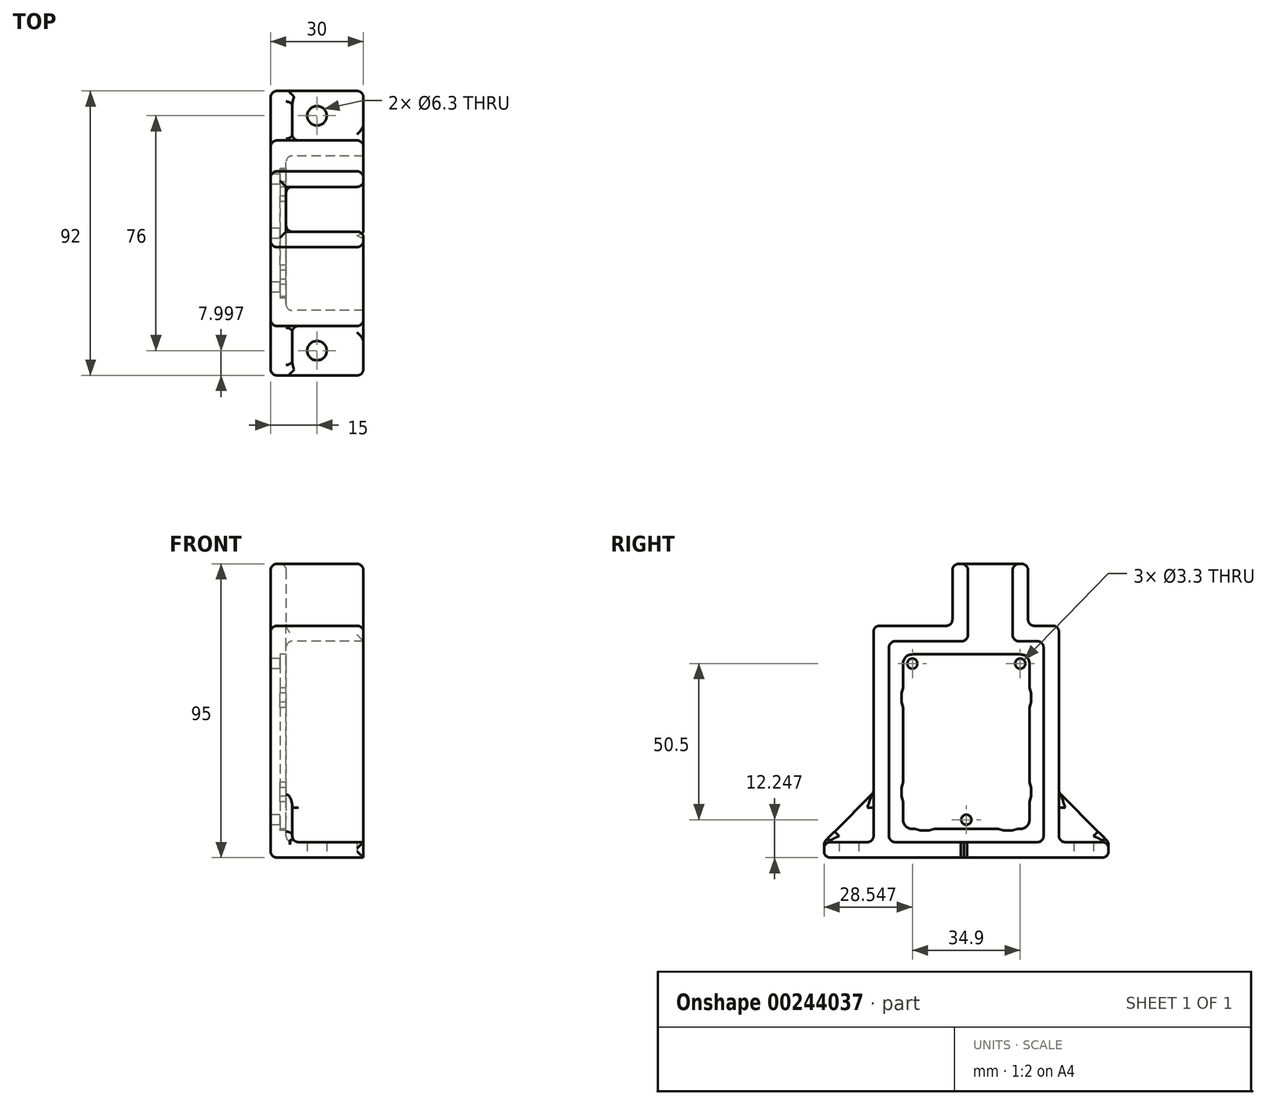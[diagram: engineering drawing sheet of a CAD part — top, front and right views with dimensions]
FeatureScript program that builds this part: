
annotation { "Feature Type Name" : "Feature", "Feature Type Description" : "" }
export const myFeature = defineFeature(function(context is Context, id is Id, definition is map)
    precondition{}
    {
        {
            var Q0;
            Q0=qCreatedBy(makeId("Right.planeOp"),FACE);
            var sketch = newSketch(context, id + "F0", { "sketchPlane" : qUnion([Q0])});
            skCircle(sketch, "E0", {"center": v(-16.66, 26.27) * mm, "radius": 3 * mm});
            skPoint(sketch, "E0.first.point", {"position": v(-14.03, 27.7) * mm});
            skPoint(sketch, "E0.second.point", {"position": v(-18.5, 23.89) * mm});
            skPoint(sketch, "E0.third.point", {"position": v(-19.66, 26.27) * mm});
            skCircle(sketch, "E1", {"center": v(-16.66, 26.27) * mm, "radius": 1.65 * mm});
            skCircle(sketch, "E2", {"center": v(18.24, 26.27) * mm, "radius": 3 * mm});
            skPoint(sketch, "E2.second.point", {"position": v(21.24, 26.27) * mm});
            skPoint(sketch, "E2.third.point", {"position": v(16.12, 24.15) * mm});
            skCircle(sketch, "E3", {"center": v(18.24, 26.27) * mm, "radius": 1.65 * mm});
            skCircle(sketch, "E4", {"center": v(0.79, -24.23) * mm, "radius": 3 * mm});
            skPoint(sketch, "E4.first.point", {"position": v(-0.78, -21.68) * mm});
            skPoint(sketch, "E4.second.point", {"position": v(3.71, -23.57) * mm});
            skPoint(sketch, "E4.third.point", {"position": v(-0.7, -26.84) * mm});
            skCircle(sketch, "E5", {"center": v(0.79, -24.23) * mm, "radius": 1.65 * mm});
            skLineSegment(sketch, "E6", {"start": v(-16.66, 26.27) * mm, "end": v(18.24, 26.27) * mm});
            skLineSegment(sketch, "E7", {"start": v(0.79, 26.27) * mm, "end": v(0.79, -24.23) * mm});
            skPoint(sketch, "E8", {"position": v(0.79, 1.02) * mm});
            skLineSegment(sketch, "E9.rect.bottom", {"start": v(30.79, 38.52) * mm, "end": v(-29.21, 38.52) * mm});
            skLineSegment(sketch, "E9.rect.top", {"start": v(30.79, -36.48) * mm, "end": v(-29.21, -36.48) * mm});
            skLineSegment(sketch, "E9.rect.left", {"start": v(30.79, 38.52) * mm, "end": v(30.79, -36.48) * mm});
            skLineSegment(sketch, "E9.rect.right", {"start": v(-29.21, 38.52) * mm, "end": v(-29.21, -36.48) * mm});
            skLineSegment(sketch, "E10.top", {"start": v(-13.71, 38.52) * mm, "end": v(0.79, 38.52) * mm});
            skLineSegment(sketch, "E11.bottom", {"start": v(6.79, 38.52) * mm, "end": v(0.79, 38.52) * mm});
            skLineSegment(sketch, "E12.bottom", {"start": v(-19.71, 38.52) * mm, "end": v(-13.71, 38.52) * mm});
            skSolve(sketch);
        }
        {
            var Q0;
            Q0=qCreatedBy(makeId("Right.planeOp"),FACE);
            var sketch = newSketch(context, id + "F1", { "sketchPlane" : qUnion([Q0])});
            skCircle(sketch, "E13", {"center": v(-16.66, 26.27) * mm, "radius": 3 * mm});
            skPoint(sketch, "E13.first.point", {"position": v(-14.03, 27.7) * mm});
            skPoint(sketch, "E13.second.point", {"position": v(-18.5, 23.89) * mm});
            skPoint(sketch, "E13.third.point", {"position": v(-19.66, 26.27) * mm});
            skCircle(sketch, "E14", {"center": v(-16.66, 26.27) * mm, "radius": 1.65 * mm});
            skLineSegment(sketch, "E15", {"start": v(-16.66, 29.27) * mm, "end": v(18.24, 29.27) * mm});
            skCircle(sketch, "E16", {"center": v(18.24, 26.27) * mm, "radius": 3 * mm});
            skPoint(sketch, "E16.second.point", {"position": v(21.24, 26.27) * mm});
            skPoint(sketch, "E16.third.point", {"position": v(16.12, 24.15) * mm});
            skCircle(sketch, "E17", {"center": v(18.24, 26.27) * mm, "radius": 1.65 * mm});
            skLineSegment(sketch, "E18", {"start": v(21.24, 26.27) * mm, "end": v(21.24, -24.23) * mm});
            skLineSegment(sketch, "E19", {"start": v(18.24, -27.23) * mm, "end": v(-16.66, -27.23) * mm});
            skLineSegment(sketch, "E20", {"start": v(-19.66, -24.23) * mm, "end": v(-19.66, 26.27) * mm});
            skCircle(sketch, "E21", {"center": v(0.79, -24.23) * mm, "radius": 3 * mm});
            skPoint(sketch, "E21.first.point", {"position": v(-0.78, -21.68) * mm});
            skPoint(sketch, "E21.second.point", {"position": v(3.71, -23.57) * mm});
            skPoint(sketch, "E21.third.point", {"position": v(-0.7, -26.84) * mm});
            skCircle(sketch, "E22", {"center": v(0.79, -24.23) * mm, "radius": 1.65 * mm});
            skCircle(sketch, "E23", {"center": v(-16.66, -24.23) * mm, "radius": 3 * mm});
            skPoint(sketch, "E23.third.point", {"position": v(-18.78, -26.35) * mm});
            skCircle(sketch, "E24", {"center": v(18.24, -24.23) * mm, "radius": 3 * mm});
            skPoint(sketch, "E24.third.point", {"position": v(20.85, -25.72) * mm});
            skLineSegment(sketch, "E25", {"start": v(12.81, -27.73) * mm, "end": v(15.66, -27.73) * mm});
            skLineSegment(sketch, "E26", {"start": v(12.81, -27.73) * mm, "end": v(11.08, -27.23) * mm});
            skLineSegment(sketch, "E27", {"start": v(15.66, -27.73) * mm, "end": v(17.4, -27.23) * mm});
            skLineSegment(sketch, "E28", {"start": v(-14.09, -27.73) * mm, "end": v(-11.24, -27.73) * mm});
            skLineSegment(sketch, "E29", {"start": v(-11.24, -27.73) * mm, "end": v(-9.5, -27.23) * mm});
            skLineSegment(sketch, "E30", {"start": v(-15.82, -27.23) * mm, "end": v(-14.09, -27.73) * mm});
            skLineSegment(sketch, "E31", {"start": v(-20.16, -13.8) * mm, "end": v(-19.66, -12.07) * mm});
            skLineSegment(sketch, "E32", {"start": v(-20.16, -13.8) * mm, "end": v(-20.16, -16.66) * mm});
            skLineSegment(sketch, "E33", {"start": v(-20.16, -16.66) * mm, "end": v(-19.66, -18.4) * mm});
            skLineSegment(sketch, "E34", {"start": v(-20.16, 16.7) * mm, "end": v(-20.16, 13.84) * mm});
            skLineSegment(sketch, "E35", {"start": v(-20.16, 13.84) * mm, "end": v(-19.66, 12.1) * mm});
            skLineSegment(sketch, "E36", {"start": v(-20.16, 16.7) * mm, "end": v(-19.66, 18.43) * mm});
            skLineSegment(sketch, "E37", {"start": v(21.74, 16.7) * mm, "end": v(21.24, 18.43) * mm});
            skLineSegment(sketch, "E38", {"start": v(21.74, 16.7) * mm, "end": v(21.74, 13.84) * mm});
            skLineSegment(sketch, "E39", {"start": v(21.74, 13.84) * mm, "end": v(21.24, 12.1) * mm});
            skLineSegment(sketch, "E40", {"start": v(21.24, -12.07) * mm, "end": v(21.74, -13.87) * mm});
            skLineSegment(sketch, "E41", {"start": v(21.74, -13.87) * mm, "end": v(21.74, -16.66) * mm});
            skLineSegment(sketch, "E42", {"start": v(21.74, -16.66) * mm, "end": v(21.24, -18.4) * mm});
            skLineSegment(sketch, "E43", {"start": v(-16.66, 26.27) * mm, "end": v(18.24, 26.27) * mm});
            skLineSegment(sketch, "E44", {"start": v(0.79, 26.27) * mm, "end": v(0.79, -24.23) * mm});
            skPoint(sketch, "E45", {"position": v(0.79, 1.02) * mm});
            skLineSegment(sketch, "E46.rect.bottom", {"start": v(30.79, 38.52) * mm, "end": v(-29.21, 38.52) * mm});
            skLineSegment(sketch, "E46.rect.top", {"start": v(30.79, -36.48) * mm, "end": v(-29.21, -36.48) * mm});
            skLineSegment(sketch, "E46.rect.left", {"start": v(30.79, 38.52) * mm, "end": v(30.79, -36.48) * mm});
            skLineSegment(sketch, "E46.rect.right", {"start": v(-29.21, 38.52) * mm, "end": v(-29.21, -36.48) * mm});
            skLineSegment(sketch, "E47.top", {"start": v(-13.71, 38.52) * mm, "end": v(0.79, 38.52) * mm});
            skLineSegment(sketch, "E48.bottom", {"start": v(6.79, 38.52) * mm, "end": v(0.79, 38.52) * mm});
            skLineSegment(sketch, "E49.bottom", {"start": v(-19.71, 38.52) * mm, "end": v(-13.71, 38.52) * mm});
            skSolve(sketch);
        }
        {
            var Q0;
            Q0 = qSketchRegion(id + "F0", true);
            var Q1;
            Q1=makeQuery(id+"F0.imprint","IMPRINT",FACE,{"disambiguationData":[TD([[makeQuery(id+"F0.imprint","IMPRINT",EDGE,{"derivedFrom":sQuery(id+"F0.wireOp",EDGE,"E4")}),1.0]])]});
            var Q2;
            Q2=makeQuery(id+"F0.imprint","IMPRINT",FACE,{"disambiguationData":[TD([[makeQuery(id+"F0.imprint","IMPRINT",EDGE,{"derivedFrom":sQuery(id+"F0.wireOp",EDGE,"E2")}),1.0]])]});
            var Q3;
            Q3=makeQuery(id+"F0.imprint","IMPRINT",FACE,{"disambiguationData":[TD([[makeQuery(id+"F0.imprint","IMPRINT",EDGE,{"derivedFrom":sQuery(id+"F0.wireOp",EDGE,"E0")}),1.0]])]});
            extrude(context, id + "F2", {"entities" : qUnion([Q0, Q1, Q2, Q3]), "offsetDistance" : 25 * mm, "depth" : 3 * mm});
        }
        {
            var Q0;
            Q0 = qSketchRegion(id + "F1", true);
            extrude(context, id + "F3", {"entities" : qUnion([Q0]), "operationType" : NewBodyOperationType.ADD, "offsetDistance" : 25 * mm, "depth" : 5 * mm});
        }
        {
            var Q0;
            Q0=makeQuery(id+"F2.opExtrude","CAP_FACE",FACE,{"disambiguationData":[OSD([sQuery(id+"F0.wireOp",EDGE,"E1"),sQuery(id+"F0.wireOp",EDGE,"E3"),sQuery(id+"F0.wireOp",EDGE,"E5"),sQuery(id+"F0.wireOp",EDGE,"E9.rect.bottom"),sQuery(id+"F0.wireOp",EDGE,"E9.rect.top"),sQuery(id+"F0.wireOp",EDGE,"E9.rect.left"),sQuery(id+"F0.wireOp",EDGE,"E9.rect.right"),sQuery(id+"F0.wireOp",EDGE,"E10.top"),sQuery(id+"F0.wireOp",EDGE,"E11.bottom"),sQuery(id+"F0.wireOp",EDGE,"E12.bottom")])],"isStart":true});
            var sketch = newSketch(context, id + "F4", { "sketchPlane" : qUnion([Q0])});
            skLineSegment(sketch, "E50.bottom", {"start": v(-30.79, 38.52) * mm, "end": v(-25.79, 38.52) * mm});
            skLineSegment(sketch, "E50.top", {"start": v(-30.79, -31.48) * mm, "end": v(-25.79, -31.48) * mm});
            skLineSegment(sketch, "E50.left", {"start": v(-30.79, 38.52) * mm, "end": v(-30.79, -31.48) * mm});
            skLineSegment(sketch, "E50.right", {"start": v(-25.79, 38.52) * mm, "end": v(-25.79, -31.48) * mm});
            skLineSegment(sketch, "E51.bottom", {"start": v(29.21, 38.52) * mm, "end": v(24.21, 38.52) * mm});
            skLineSegment(sketch, "E51.top", {"start": v(29.21, -31.48) * mm, "end": v(24.21, -31.48) * mm});
            skLineSegment(sketch, "E51.left", {"start": v(29.21, 38.52) * mm, "end": v(29.21, -31.48) * mm});
            skLineSegment(sketch, "E51.right", {"start": v(24.21, 38.52) * mm, "end": v(24.21, -31.48) * mm});
            skLineSegment(sketch, "E52.bottom", {"start": v(-30.79, -31.48) * mm, "end": v(29.21, -31.48) * mm});
            skLineSegment(sketch, "E52.top", {"start": v(-30.79, -36.48) * mm, "end": v(29.21, -36.48) * mm});
            skLineSegment(sketch, "E52.left", {"start": v(-30.79, -36.48) * mm, "end": v(-30.79, -31.48) * mm});
            skLineSegment(sketch, "E52.right", {"start": v(29.21, -36.48) * mm, "end": v(29.21, -31.48) * mm});
            skLineSegment(sketch, "E53.bottom", {"start": v(-30.79, 38.52) * mm, "end": v(-15.79, 38.52) * mm});
            skLineSegment(sketch, "E53.top", {"start": v(-30.79, 33.52) * mm, "end": v(-15.79, 33.52) * mm});
            skLineSegment(sketch, "E53.left", {"start": v(-30.79, 33.52) * mm, "end": v(-30.79, 38.52) * mm});
            skLineSegment(sketch, "E53.right", {"start": v(-15.79, 33.52) * mm, "end": v(-15.79, 38.52) * mm});
            skLineSegment(sketch, "E54.bottom", {"start": v(-15.79, 38.52) * mm, "end": v(-20.79, 38.52) * mm});
            skLineSegment(sketch, "E54.top", {"start": v(-15.79, 58.52) * mm, "end": v(-20.79, 58.52) * mm});
            skLineSegment(sketch, "E54.left", {"start": v(-15.79, 38.52) * mm, "end": v(-15.79, 58.52) * mm});
            skLineSegment(sketch, "E54.right", {"start": v(-20.79, 38.52) * mm, "end": v(-20.79, 58.52) * mm});
            skLineSegment(sketch, "E55.bottom", {"start": v(29.21, 38.52) * mm, "end": v(-1.29, 38.52) * mm});
            skLineSegment(sketch, "E55.top", {"start": v(29.21, 33.52) * mm, "end": v(-1.29, 33.52) * mm});
            skLineSegment(sketch, "E55.left", {"start": v(29.21, 38.52) * mm, "end": v(29.21, 33.52) * mm});
            skLineSegment(sketch, "E55.right", {"start": v(-1.29, 38.52) * mm, "end": v(-1.29, 33.52) * mm});
            skLineSegment(sketch, "E56.bottom", {"start": v(-1.29, 33.52) * mm, "end": v(3.71, 33.52) * mm});
            skLineSegment(sketch, "E56.top", {"start": v(-1.29, 58.52) * mm, "end": v(3.71, 58.52) * mm});
            skLineSegment(sketch, "E56.left", {"start": v(-1.29, 33.52) * mm, "end": v(-1.29, 58.52) * mm});
            skLineSegment(sketch, "E56.right", {"start": v(3.71, 33.52) * mm, "end": v(3.71, 58.52) * mm});
            skLineSegment(sketch, "E57.bottom", {"start": v(-15.79, 58.52) * mm, "end": v(-1.29, 58.52) * mm});
            skLineSegment(sketch, "E57.top", {"start": v(-15.79, 38.52) * mm, "end": v(-1.29, 38.52) * mm});
            skLineSegment(sketch, "E57.left", {"start": v(-15.79, 58.52) * mm, "end": v(-15.79, 38.52) * mm});
            skLineSegment(sketch, "E57.right", {"start": v(-1.29, 58.52) * mm, "end": v(-1.29, 38.52) * mm});
            skSolve(sketch);
        }
        {
            var Q0;
            {var subQ3=sQuery(id+"F4.wireOp",EDGE,"E53.right");Q0=makeQuery(id+"F4.imprint","IMPRINT",FACE,{"disambiguationData":[TD([[makeQuery(id+"F4.imprint","IMPRINT",EDGE,{"derivedFrom":subQ3}),1.0]])]});}
            var Q1;
            {var subQ0=sQuery(id+"F4.wireOp",EDGE,"E50.bottom");Q1=makeQuery(id+"F4.imprint","IMPRINT",FACE,{"disambiguationData":[TD([[makeQuery(id+"F4.imprint","IMPRINT",EDGE,{"derivedFrom":subQ0}),-1.0]])]});}
            var Q2;
            {var subQ0=sQuery(id+"F4.wireOp",EDGE,"E50.top");Q2=makeQuery(id+"F4.imprint","IMPRINT",FACE,{"disambiguationData":[TD([[makeQuery(id+"F4.imprint","IMPRINT",EDGE,{"derivedFrom":subQ0}),1.0]])]});}
            var Q3;
            Q3=makeQuery(id+"F4.imprint","IMPRINT",FACE,{"disambiguationData":[TD([[makeQuery(id+"F4.imprint","IMPRINT",EDGE,{"derivedFrom":sQuery(id+"F4.wireOp",EDGE,"E54.top")}),1.0]])]});
            var Q4;
            {var subQ4=sQuery(id+"F4.wireOp",EDGE,"E56.top");Q4=makeQuery(id+"F4.imprint","IMPRINT",FACE,{"disambiguationData":[TD([[makeQuery(id+"F4.imprint","IMPRINT",EDGE,{"derivedFrom":subQ4}),-1.0]])]});}
            var Q5;
            {var subQ0=sQuery(id+"F4.wireOp",EDGE,"E55.right");Q5=makeQuery(id+"F4.imprint","IMPRINT",FACE,{"disambiguationData":[TD([[makeQuery(id+"F4.imprint","IMPRINT",EDGE,{"derivedFrom":subQ0}),1.0]])]});}
            var Q6;
            {var subQ1=sQuery(id+"F4.wireOp",EDGE,"E51.right");var subQ3=sQuery(id+"F4.wireOp",EDGE,"E55.top");var subQ4=makeQuery(id+"F4.imprint","INTERSECT",VERTEX,{"derivedFrom":[subQ1,subQ3]});Q6=makeQuery(id+"F4.imprint","IMPRINT",FACE,{"disambiguationData":[TD([[makeQuery(id+"F4.imprint","IMPRINT",EDGE,{"disambiguationData":[TD([[subQ4,-1.0]])],"derivedFrom":subQ3}),-1.0]])]});}
            var Q7;
            {var subQ0=sQuery(id+"F4.wireOp",EDGE,"E51.top");Q7=makeQuery(id+"F4.imprint","IMPRINT",FACE,{"disambiguationData":[TD([[makeQuery(id+"F4.imprint","IMPRINT",EDGE,{"derivedFrom":subQ0}),-1.0]])]});}
            var Q8;
            Q8=makeQuery(id+"F4.imprint","IMPRINT",FACE,{"disambiguationData":[TD([[makeQuery(id+"F4.imprint","IMPRINT",EDGE,{"derivedFrom":sQuery(id+"F4.wireOp",EDGE,"E50.top")}),-1.0]])]});
            var Q9;
            {var subQ0=sQuery(id+"F4.wireOp",EDGE,"E51.bottom");Q9=makeQuery(id+"F4.imprint","IMPRINT",FACE,{"disambiguationData":[TD([[makeQuery(id+"F4.imprint","IMPRINT",EDGE,{"derivedFrom":subQ0}),-1.0]])]});}
            extrude(context, id + "F5", {"entities" : qUnion([Q0, Q1, Q2, Q3, Q4, Q5, Q6, Q7, Q8, Q9]), "operationType" : NewBodyOperationType.ADD, "oppositeDirection" : true, "depth" : 30 * mm, "offsetDistance" : 25 * mm});
        }
        {
            var Q0;
            Q0=makeQuery(id+"F4.imprint","IMPRINT",FACE,{"disambiguationData":[TD([[makeQuery(id+"F4.imprint","IMPRINT",EDGE,{"derivedFrom":sQuery(id+"F4.wireOp",EDGE,"E54.left")}),-1.0]])]});
            extrude(context, id + "F6", {"entities" : qUnion([Q0]), "operationType" : NewBodyOperationType.ADD, "oppositeDirection" : true, "depth" : 5 * mm, "offsetDistance" : 25 * mm});
        }
        {
            var Q0;
            Q0=makeQuery(id+"F5.boolean.opBoolean","MERGE",FACE,{"derivedFrom":[makeQuery(id+"F3.boolean.opBoolean","MERGE",FACE,{"derivedFrom":[makeQuery(id+"F2.opExtrude","SWEPT_FACE",FACE,{"disambiguationData":[OSD([sQuery(id+"F0.wireOp",EDGE,"E9.rect.top")])]}),makeQuery(id+"F3.opExtrude","SWEPT_FACE",FACE,{"disambiguationData":[OSD([sQuery(id+"F1.wireOp",EDGE,"E46.rect.top")])]})]}),makeQuery(id+"F5.opExtrude","SWEPT_FACE",FACE,{"disambiguationData":[OSD([sQuery(id+"F4.wireOp",EDGE,"E52.top")])]})]});
            var sketch = newSketch(context, id + "F7", { "sketchPlane" : qUnion([Q0])});
            skLineSegment(sketch, "E58.bottom", {"start": v(30, 29.21) * mm, "end": v(0, 29.21) * mm});
            skLineSegment(sketch, "E58.top", {"start": v(30, 45.21) * mm, "end": v(0, 45.21) * mm});
            skLineSegment(sketch, "E58.left", {"start": v(30, 29.21) * mm, "end": v(30, 45.21) * mm});
            skLineSegment(sketch, "E58.right", {"start": v(0, 29.21) * mm, "end": v(0, 45.21) * mm});
            skLineSegment(sketch, "E59.bottom", {"start": v(0, -30.79) * mm, "end": v(30, -30.79) * mm});
            skLineSegment(sketch, "E59.top", {"start": v(0, -46.79) * mm, "end": v(30, -46.79) * mm});
            skLineSegment(sketch, "E59.left", {"start": v(0, -30.79) * mm, "end": v(0, -46.79) * mm});
            skLineSegment(sketch, "E59.right", {"start": v(30, -30.79) * mm, "end": v(30, -46.79) * mm});
            skSolve(sketch);
        }
        {
            var Q0;
            Q0=makeQuery(id+"F7.imprint","IMPRINT",FACE,{"disambiguationData":[TD([[makeQuery(id+"F7.imprint","IMPRINT",EDGE,{"derivedFrom":sQuery(id+"F7.wireOp",EDGE,"E58.bottom")}),-1.0]])]});
            var Q1;
            Q1=makeQuery(id+"F7.imprint","IMPRINT",FACE,{"disambiguationData":[TD([[makeQuery(id+"F7.imprint","IMPRINT",EDGE,{"derivedFrom":sQuery(id+"F7.wireOp",EDGE,"E59.bottom")}),1.0]])]});
            var Q2;
            Q2=makeQuery(id+"F5.opExtrude","SWEPT_FACE",FACE,{"disambiguationData":[OSD([sQuery(id+"F4.wireOp",EDGE,"E52.bottom")])]});
            extrude(context, id + "F8", {"entities" : qUnion([Q0, Q1]), "operationType" : NewBodyOperationType.ADD, "endBound" : BoundingType.UP_TO_SURFACE, "oppositeDirection" : true, "depth" : 25 * mm, "endBoundEntityFace" : qUnion([Q2]), "offsetDistance" : 25 * mm});
        }
        {
            var Q0;
            Q0=makeQuery(id+"F8.boolean.opBoolean","MERGE",FACE,{"derivedFrom":[makeQuery(id+"F5.boolean.opBoolean","MERGE",FACE,{"derivedFrom":[makeQuery(id+"F3.boolean.opBoolean","MERGE",FACE,{"derivedFrom":[makeQuery(id+"F2.opExtrude","SWEPT_FACE",FACE,{"disambiguationData":[OSD([sQuery(id+"F0.wireOp",EDGE,"E9.rect.top")])]}),makeQuery(id+"F3.opExtrude","SWEPT_FACE",FACE,{"disambiguationData":[OSD([sQuery(id+"F1.wireOp",EDGE,"E46.rect.top")])]})]}),makeQuery(id+"F5.opExtrude","SWEPT_FACE",FACE,{"disambiguationData":[OSD([sQuery(id+"F4.wireOp",EDGE,"E52.top")])]})]}),makeQuery(id+"F8.opExtrude","CAP_FACE",FACE,{"disambiguationData":[OSD([sQuery(id+"F7.wireOp",EDGE,"E58.bottom"),sQuery(id+"F7.wireOp",EDGE,"E58.top"),sQuery(id+"F7.wireOp",EDGE,"E58.left"),sQuery(id+"F7.wireOp",EDGE,"E58.right")])],"isStart":true}),makeQuery(id+"F8.opExtrude","CAP_FACE",FACE,{"disambiguationData":[OSD([sQuery(id+"F7.wireOp",EDGE,"E59.bottom"),sQuery(id+"F7.wireOp",EDGE,"E59.top"),sQuery(id+"F7.wireOp",EDGE,"E59.left"),sQuery(id+"F7.wireOp",EDGE,"E59.right")])],"isStart":true})]});
            var sketch = newSketch(context, id + "F9", { "sketchPlane" : qUnion([Q0])});
            skCircle(sketch, "E60", {"center": v(15, 37.21) * mm, "radius": 3.15 * mm});
            skPoint(sketch, "E60.centerSnap0", {"position": v(15, 45.21) * mm});
            skCircle(sketch, "E61", {"center": v(15, -38.79) * mm, "radius": 3.15 * mm});
            skPoint(sketch, "E61.centerSnap0", {"position": v(15, -46.79) * mm});
            skSolve(sketch);
        }
        {
            var Q0;
            Q0=makeQuery(id+"F9.imprint","IMPRINT",FACE,{"disambiguationData":[TD([[makeQuery(id+"F9.imprint","IMPRINT",EDGE,{"derivedFrom":sQuery(id+"F9.wireOp",EDGE,"E60")}),1.0]])]});
            var Q1;
            Q1=makeQuery(id+"F9.imprint","IMPRINT",FACE,{"disambiguationData":[TD([[makeQuery(id+"F9.imprint","IMPRINT",EDGE,{"derivedFrom":sQuery(id+"F9.wireOp",EDGE,"E61")}),1.0]])]});
            extrude(context, id + "F10", {"entities" : qUnion([Q0, Q1]), "operationType" : NewBodyOperationType.REMOVE, "oppositeDirection" : true, "depth" : 25 * mm, "offsetDistance" : 25 * mm});
        }
        {
            var Q0;
            Q0=makeQuery(id+"F8.boolean.opBoolean","MERGE",FACE,{"derivedFrom":[makeQuery(id+"F5.boolean.opBoolean","MERGE",FACE,{"derivedFrom":[makeQuery(id+"F3.boolean.opBoolean","MERGE",FACE,{"derivedFrom":[makeQuery(id+"F2.opExtrude","SWEPT_FACE",FACE,{"disambiguationData":[OSD([sQuery(id+"F0.wireOp",EDGE,"E9.rect.top")])]}),makeQuery(id+"F3.opExtrude","SWEPT_FACE",FACE,{"disambiguationData":[OSD([sQuery(id+"F1.wireOp",EDGE,"E46.rect.top")])]})]}),makeQuery(id+"F5.opExtrude","SWEPT_FACE",FACE,{"disambiguationData":[OSD([sQuery(id+"F4.wireOp",EDGE,"E52.top")])]})]}),makeQuery(id+"F8.opExtrude","CAP_FACE",FACE,{"disambiguationData":[OSD([sQuery(id+"F7.wireOp",EDGE,"E58.bottom"),sQuery(id+"F7.wireOp",EDGE,"E58.top"),sQuery(id+"F7.wireOp",EDGE,"E58.left"),sQuery(id+"F7.wireOp",EDGE,"E58.right")])],"isStart":true}),makeQuery(id+"F8.opExtrude","CAP_FACE",FACE,{"disambiguationData":[OSD([sQuery(id+"F7.wireOp",EDGE,"E59.bottom"),sQuery(id+"F7.wireOp",EDGE,"E59.top"),sQuery(id+"F7.wireOp",EDGE,"E59.left"),sQuery(id+"F7.wireOp",EDGE,"E59.right")])],"isStart":true})]});
            var sketch = newSketch(context, id + "F11", { "sketchPlane" : qUnion([Q0])});
            skLineSegment(sketch, "E62", {"start": v(30, 1) * mm, "end": v(28, 0) * mm});
            skLineSegment(sketch, "E63", {"start": v(28, 0) * mm, "end": v(30, -1) * mm});
            skLineSegment(sketch, "E64", {"start": v(30, -1) * mm, "end": v(30, 1) * mm});
            skSolve(sketch);
        }
        {
            var Q0;
            Q0=makeQuery(id+"F11.imprint","IMPRINT",FACE,{"disambiguationData":[TD([[makeQuery(id+"F11.imprint","IMPRINT",EDGE,{"derivedFrom":sQuery(id+"F11.wireOp",EDGE,"E62")}),1.0]])]});
            extrude(context, id + "F12", {"entities" : qUnion([Q0]), "operationType" : NewBodyOperationType.REMOVE, "oppositeDirection" : true, "depth" : 25 * mm, "offsetDistance" : 25 * mm});
        }
        {
            var Q0;
            {var subQ0=sQuery(id+"F4.wireOp",EDGE,"E56.left");var subQ1=sQuery(id+"F4.wireOp",EDGE,"E54.left");Q0=makeQuery(id+"F8.boolean.opBoolean","MERGE",FACE,{"derivedFrom":[makeQuery(id+"F6.boolean.opBoolean","MERGE",FACE,{"derivedFrom":[makeQuery(id+"F5.boolean.opBoolean","MERGE",FACE,{"derivedFrom":[makeQuery(id+"F2.opExtrude","CAP_FACE",FACE,{"disambiguationData":[OSD([sQuery(id+"F0.wireOp",EDGE,"E1"),sQuery(id+"F0.wireOp",EDGE,"E3"),sQuery(id+"F0.wireOp",EDGE,"E5"),sQuery(id+"F0.wireOp",EDGE,"E9.rect.bottom"),sQuery(id+"F0.wireOp",EDGE,"E9.rect.top"),sQuery(id+"F0.wireOp",EDGE,"E9.rect.left"),sQuery(id+"F0.wireOp",EDGE,"E9.rect.right"),sQuery(id+"F0.wireOp",EDGE,"E10.top"),sQuery(id+"F0.wireOp",EDGE,"E11.bottom"),sQuery(id+"F0.wireOp",EDGE,"E12.bottom")])],"isStart":true}),makeQuery(id+"F5.opExtrude","CAP_FACE",FACE,{"disambiguationData":[OSD([sQuery(id+"F4.wireOp",EDGE,"E50.bottom"),sQuery(id+"F4.wireOp",EDGE,"E50.left"),sQuery(id+"F4.wireOp",EDGE,"E50.right"),sQuery(id+"F4.wireOp",EDGE,"E51.bottom"),sQuery(id+"F4.wireOp",EDGE,"E51.left"),sQuery(id+"F4.wireOp",EDGE,"E51.right"),sQuery(id+"F4.wireOp",EDGE,"E52.bottom"),sQuery(id+"F4.wireOp",EDGE,"E52.top"),sQuery(id+"F4.wireOp",EDGE,"E52.left"),sQuery(id+"F4.wireOp",EDGE,"E52.right"),sQuery(id+"F4.wireOp",EDGE,"E53.bottom"),sQuery(id+"F4.wireOp",EDGE,"E53.top"),sQuery(id+"F4.wireOp",EDGE,"E53.right"),sQuery(id+"F4.wireOp",EDGE,"E54.top"),subQ1,sQuery(id+"F4.wireOp",EDGE,"E54.right"),sQuery(id+"F4.wireOp",EDGE,"E55.bottom"),sQuery(id+"F4.wireOp",EDGE,"E55.top"),sQuery(id+"F4.wireOp",EDGE,"E55.right"),sQuery(id+"F4.wireOp",EDGE,"E56.top"),subQ0,sQuery(id+"F4.wireOp",EDGE,"E56.right")])],"isStart":true})]}),makeQuery(id+"F6.opExtrude","CAP_FACE",FACE,{"disambiguationData":[OSD([subQ1,subQ0,sQuery(id+"F4.wireOp",EDGE,"E57.bottom"),sQuery(id+"F4.wireOp",EDGE,"E57.top")])],"isStart":true})]}),makeQuery(id+"F8.opExtrude","SWEPT_FACE",FACE,{"disambiguationData":[OSD([sQuery(id+"F7.wireOp",EDGE,"E58.right")])]}),makeQuery(id+"F8.opExtrude","SWEPT_FACE",FACE,{"disambiguationData":[OSD([sQuery(id+"F7.wireOp",EDGE,"E59.left")])]})]});}
            var sketch = newSketch(context, id + "F13", { "sketchPlane" : qUnion([Q0])});
            skLineSegment(sketch, "E65", {"start": v(-46.79, -31.48) * mm, "end": v(-30.79, -15.48) * mm});
            skLineSegment(sketch, "E66", {"start": v(-30.79, -15.48) * mm, "end": v(-30.79, -31.48) * mm});
            skLineSegment(sketch, "E67", {"start": v(-30.79, -31.48) * mm, "end": v(-46.79, -31.48) * mm});
            skLineSegment(sketch, "E68", {"start": v(29.21, -31.48) * mm, "end": v(29.21, -15.48) * mm});
            skLineSegment(sketch, "E69", {"start": v(29.21, -15.48) * mm, "end": v(45.21, -31.48) * mm});
            skLineSegment(sketch, "E70", {"start": v(45.21, -31.48) * mm, "end": v(29.21, -31.48) * mm});
            skSolve(sketch);
        }
        {
            var Q0;
            Q0 = qSketchRegion(id + "F13", true);
            extrude(context, id + "F14", {"entities" : qUnion([Q0]), "operationType" : NewBodyOperationType.ADD, "oppositeDirection" : true, "depth" : 7 * mm, "offsetDistance" : 25 * mm});
        }
        {
            var Q0;
            {var subQ0=sQuery(id+"F4.wireOp",EDGE,"E56.left");var subQ1=sQuery(id+"F4.wireOp",EDGE,"E54.left");Q0=makeQuery(id+"F14.boolean.opBoolean","MERGE",FACE,{"derivedFrom":[makeQuery(id+"F8.boolean.opBoolean","MERGE",FACE,{"derivedFrom":[makeQuery(id+"F6.boolean.opBoolean","MERGE",FACE,{"derivedFrom":[makeQuery(id+"F5.boolean.opBoolean","MERGE",FACE,{"derivedFrom":[makeQuery(id+"F2.opExtrude","CAP_FACE",FACE,{"disambiguationData":[OSD([sQuery(id+"F0.wireOp",EDGE,"E1"),sQuery(id+"F0.wireOp",EDGE,"E3"),sQuery(id+"F0.wireOp",EDGE,"E5"),sQuery(id+"F0.wireOp",EDGE,"E9.rect.bottom"),sQuery(id+"F0.wireOp",EDGE,"E9.rect.top"),sQuery(id+"F0.wireOp",EDGE,"E9.rect.left"),sQuery(id+"F0.wireOp",EDGE,"E9.rect.right"),sQuery(id+"F0.wireOp",EDGE,"E10.top"),sQuery(id+"F0.wireOp",EDGE,"E11.bottom"),sQuery(id+"F0.wireOp",EDGE,"E12.bottom")])],"isStart":true}),makeQuery(id+"F5.opExtrude","CAP_FACE",FACE,{"disambiguationData":[OSD([sQuery(id+"F4.wireOp",EDGE,"E50.bottom"),sQuery(id+"F4.wireOp",EDGE,"E50.left"),sQuery(id+"F4.wireOp",EDGE,"E50.right"),sQuery(id+"F4.wireOp",EDGE,"E51.bottom"),sQuery(id+"F4.wireOp",EDGE,"E51.left"),sQuery(id+"F4.wireOp",EDGE,"E51.right"),sQuery(id+"F4.wireOp",EDGE,"E52.bottom"),sQuery(id+"F4.wireOp",EDGE,"E52.top"),sQuery(id+"F4.wireOp",EDGE,"E52.left"),sQuery(id+"F4.wireOp",EDGE,"E52.right"),sQuery(id+"F4.wireOp",EDGE,"E53.bottom"),sQuery(id+"F4.wireOp",EDGE,"E53.top"),sQuery(id+"F4.wireOp",EDGE,"E53.right"),sQuery(id+"F4.wireOp",EDGE,"E54.top"),subQ1,sQuery(id+"F4.wireOp",EDGE,"E54.right"),sQuery(id+"F4.wireOp",EDGE,"E55.bottom"),sQuery(id+"F4.wireOp",EDGE,"E55.top"),sQuery(id+"F4.wireOp",EDGE,"E55.right"),sQuery(id+"F4.wireOp",EDGE,"E56.top"),subQ0,sQuery(id+"F4.wireOp",EDGE,"E56.right")])],"isStart":true})]}),makeQuery(id+"F6.opExtrude","CAP_FACE",FACE,{"disambiguationData":[OSD([subQ1,subQ0,sQuery(id+"F4.wireOp",EDGE,"E57.bottom"),sQuery(id+"F4.wireOp",EDGE,"E57.top")])],"isStart":true})]}),makeQuery(id+"F8.opExtrude","SWEPT_FACE",FACE,{"disambiguationData":[OSD([sQuery(id+"F7.wireOp",EDGE,"E58.right")])]}),makeQuery(id+"F8.opExtrude","SWEPT_FACE",FACE,{"disambiguationData":[OSD([sQuery(id+"F7.wireOp",EDGE,"E59.left")])]})]}),makeQuery(id+"F14.opExtrude","CAP_FACE",FACE,{"disambiguationData":[OSD([sQuery(id+"F13.wireOp",EDGE,"E65"),sQuery(id+"F13.wireOp",EDGE,"E66"),sQuery(id+"F13.wireOp",EDGE,"E67")])],"isStart":true}),makeQuery(id+"F14.opExtrude","CAP_FACE",FACE,{"disambiguationData":[OSD([sQuery(id+"F13.wireOp",EDGE,"E68"),sQuery(id+"F13.wireOp",EDGE,"E69"),sQuery(id+"F13.wireOp",EDGE,"E70")])],"isStart":true})]});}
            cPlane(context, id + "F15", {"entities" : qUnion([Q0]), "cplaneType" : CPlaneType.OFFSET, "offset" : 15 * mm, "oppositeDirection" : true, "width" : 150 * mm, "height" : 150 * mm});
        }
        {
            var Q0;
            Q0=makeQuery(id+"F3BZSZNoRLu20LP_1.1.F14.opExtrude","SWEPT_FACE",FACE,{"disambiguationData":[OSD([sQuery(id+"F13.wireOp",EDGE,"E65")])]});
            var Q1;
            Q1=makeQuery(id+"F14.opExtrude","SWEPT_FACE",FACE,{"disambiguationData":[OSD([sQuery(id+"F13.wireOp",EDGE,"E65")])]});
            var Q2;
            Q2=makeQuery(id+"F8.opExtrude","SWEPT_FACE",FACE,{"disambiguationData":[OSD([sQuery(id+"F7.wireOp",EDGE,"E59.top")])]});
            var Q3;
            Q3=makeQuery(id+"F5.boolean.opBoolean","MERGE",FACE,{"derivedFrom":[makeQuery(id+"F3.boolean.opBoolean","MERGE",FACE,{"derivedFrom":[makeQuery(id+"F2.opExtrude","SWEPT_FACE",FACE,{"disambiguationData":[OSD([sQuery(id+"F0.wireOp",EDGE,"E9.rect.left")])]}),makeQuery(id+"F3.opExtrude","SWEPT_FACE",FACE,{"disambiguationData":[OSD([sQuery(id+"F1.wireOp",EDGE,"E46.rect.left")])]})]}),makeQuery(id+"F5.opExtrude","SWEPT_FACE",FACE,{"disambiguationData":[OSD([sQuery(id+"F4.wireOp",EDGE,"E50.left"),sQuery(id+"F4.wireOp",EDGE,"E52.left")])]})]});
            var Q4;
            Q4=makeQuery(id+"F14.opExtrude","CAP_FACE",FACE,{"disambiguationData":[OSD([sQuery(id+"F13.wireOp",EDGE,"E65"),sQuery(id+"F13.wireOp",EDGE,"E66"),sQuery(id+"F13.wireOp",EDGE,"E67")])],"isStart":false});
            var Q5;
            Q5=makeQuery(id+"F3BZSZNoRLu20LP_1.1.F14.opExtrude","CAP_EDGE",EDGE,{"disambiguationData":[OSD([sQuery(id+"F13.wireOp",EDGE,"E67")])],"isStart":false});
            var Q6;
            Q6=makeQuery(id+"F5.opExtrude","SWEPT_EDGE",EDGE,{"disambiguationData":[OSD([sQuery(id+"F4.wireOp",EDGE,"E53.bottom"),sQuery(id+"F4.wireOp",EDGE,"E54.right")])]});
            var Q7;
            Q7=makeQuery(id+"F5.opExtrude","SWEPT_FACE",FACE,{"disambiguationData":[OSD([sQuery(id+"F4.wireOp",EDGE,"E54.right")])]});
            var Q8;
            Q8=makeQuery(id+"F5.boolean.opBoolean","MERGE",FACE,{"derivedFrom":[makeQuery(id+"F3.boolean.opBoolean","MERGE",FACE,{"derivedFrom":[makeQuery(id+"F2.opExtrude","SWEPT_FACE",FACE,{"disambiguationData":[OSD([sQuery(id+"F0.wireOp",EDGE,"E9.rect.bottom"),sQuery(id+"F0.wireOp",EDGE,"E10.top"),sQuery(id+"F0.wireOp",EDGE,"E11.bottom"),sQuery(id+"F0.wireOp",EDGE,"E12.bottom")])]}),makeQuery(id+"F3.opExtrude","SWEPT_FACE",FACE,{"disambiguationData":[OSD([sQuery(id+"F1.wireOp",EDGE,"E46.rect.bottom"),sQuery(id+"F1.wireOp",EDGE,"E47.top"),sQuery(id+"F1.wireOp",EDGE,"E48.bottom"),sQuery(id+"F1.wireOp",EDGE,"E49.bottom")])]})]}),makeQuery(id+"F5.opExtrude","SWEPT_FACE",FACE,{"disambiguationData":[OSD([sQuery(id+"F4.wireOp",EDGE,"E50.bottom"),sQuery(id+"F4.wireOp",EDGE,"E53.bottom")])]})]});
            var Q9;
            Q9=makeQuery(id+"F6.boolean.opBoolean","MERGE",FACE,{"derivedFrom":[makeQuery(id+"F5.opExtrude","SWEPT_FACE",FACE,{"disambiguationData":[OSD([sQuery(id+"F4.wireOp",EDGE,"E54.top")])]}),makeQuery(id+"F5.opExtrude","SWEPT_FACE",FACE,{"disambiguationData":[OSD([sQuery(id+"F4.wireOp",EDGE,"E56.top")])]}),makeQuery(id+"F6.opExtrude","SWEPT_FACE",FACE,{"disambiguationData":[OSD([sQuery(id+"F4.wireOp",EDGE,"E57.bottom")])]})]});
            var Q10;
            Q10=makeQuery(id+"F5.boolean.opBoolean","MERGE",FACE,{"derivedFrom":[makeQuery(id+"F3.boolean.opBoolean","MERGE",FACE,{"derivedFrom":[makeQuery(id+"F2.opExtrude","SWEPT_FACE",FACE,{"disambiguationData":[OSD([sQuery(id+"F0.wireOp",EDGE,"E9.rect.bottom"),sQuery(id+"F0.wireOp",EDGE,"E10.top"),sQuery(id+"F0.wireOp",EDGE,"E11.bottom"),sQuery(id+"F0.wireOp",EDGE,"E12.bottom")])]}),makeQuery(id+"F3.opExtrude","SWEPT_FACE",FACE,{"disambiguationData":[OSD([sQuery(id+"F1.wireOp",EDGE,"E46.rect.bottom"),sQuery(id+"F1.wireOp",EDGE,"E47.top"),sQuery(id+"F1.wireOp",EDGE,"E48.bottom"),sQuery(id+"F1.wireOp",EDGE,"E49.bottom")])]})]}),makeQuery(id+"F5.opExtrude","SWEPT_FACE",FACE,{"disambiguationData":[OSD([sQuery(id+"F4.wireOp",EDGE,"E51.bottom"),sQuery(id+"F4.wireOp",EDGE,"E55.bottom")])]})]});
            var Q11;
            Q11=makeQuery(id+"F5.opExtrude","SWEPT_FACE",FACE,{"disambiguationData":[OSD([sQuery(id+"F4.wireOp",EDGE,"E56.right")])]});
            var Q12;
            Q12=makeQuery(id+"F5.boolean.opBoolean","MERGE",FACE,{"derivedFrom":[makeQuery(id+"F3.boolean.opBoolean","MERGE",FACE,{"derivedFrom":[makeQuery(id+"F2.opExtrude","SWEPT_FACE",FACE,{"disambiguationData":[OSD([sQuery(id+"F0.wireOp",EDGE,"E9.rect.right")])]}),makeQuery(id+"F3.opExtrude","SWEPT_FACE",FACE,{"disambiguationData":[OSD([sQuery(id+"F1.wireOp",EDGE,"E46.rect.right")])]})]}),makeQuery(id+"F5.opExtrude","SWEPT_FACE",FACE,{"disambiguationData":[OSD([sQuery(id+"F4.wireOp",EDGE,"E51.left"),sQuery(id+"F4.wireOp",EDGE,"E52.right")])]})]});
            var Q13;
            Q13=makeQuery(id+"F14.opExtrude","CAP_FACE",FACE,{"disambiguationData":[OSD([sQuery(id+"F13.wireOp",EDGE,"E68"),sQuery(id+"F13.wireOp",EDGE,"E69"),sQuery(id+"F13.wireOp",EDGE,"E70")])],"isStart":false});
            var Q14;
            Q14=makeQuery(id+"F14.opExtrude","SWEPT_FACE",FACE,{"disambiguationData":[OSD([sQuery(id+"F13.wireOp",EDGE,"E69")])]});
            var Q15;
            Q15=makeQuery(id+"F3BZSZNoRLu20LP_1.1.F14.opExtrude","SWEPT_FACE",FACE,{"disambiguationData":[OSD([sQuery(id+"F13.wireOp",EDGE,"E69")])]});
            var Q16;
            Q16=makeQuery(id+"F8.opExtrude","SWEPT_FACE",FACE,{"disambiguationData":[OSD([sQuery(id+"F7.wireOp",EDGE,"E58.top")])]});
            var Q17;
            Q17=makeQuery(id+"F8.boolean.opBoolean","MERGE",EDGE,{"derivedFrom":[makeQuery(id+"F2.opExtrude","CAP_EDGE",EDGE,{"disambiguationData":[OSD([sQuery(id+"F0.wireOp",EDGE,"E9.rect.top")])],"isStart":true}),makeQuery(id+"F8.opExtrude","CAP_EDGE",EDGE,{"disambiguationData":[OSD([sQuery(id+"F7.wireOp",EDGE,"E58.right")])],"isStart":true}),makeQuery(id+"F8.opExtrude","CAP_EDGE",EDGE,{"disambiguationData":[OSD([sQuery(id+"F7.wireOp",EDGE,"E59.left")])],"isStart":true})]});
            var Q18;
            Q18=makeQuery(id+"F5.opExtrude","SWEPT_EDGE",EDGE,{"disambiguationData":[OSD([sQuery(id+"F4.wireOp",EDGE,"E51.top"),sQuery(id+"F4.wireOp",EDGE,"E51.right"),sQuery(id+"F4.wireOp",EDGE,"E52.bottom")])]});
            var Q19;
            Q19=makeQuery(id+"F5.opExtrude","SWEPT_EDGE",EDGE,{"disambiguationData":[OSD([sQuery(id+"F4.wireOp",EDGE,"E51.right"),sQuery(id+"F4.wireOp",EDGE,"E55.top")])]});
            var Q20;
            Q20=makeQuery(id+"F5.opExtrude","SWEPT_EDGE",EDGE,{"disambiguationData":[OSD([sQuery(id+"F4.wireOp",EDGE,"E50.right"),sQuery(id+"F4.wireOp",EDGE,"E53.top")])]});
            var Q21;
            Q21=makeQuery(id+"F5.boolean.opBoolean","INTERSECT",EDGE,{"derivedFrom":[makeQuery(id+"F3.opExtrude","CAP_FACE",FACE,{"disambiguationData":[OSD([sQuery(id+"F1.wireOp",EDGE,"E13"),sQuery(id+"F1.wireOp",EDGE,"E15"),sQuery(id+"F1.wireOp",EDGE,"E16"),sQuery(id+"F1.wireOp",EDGE,"E18"),sQuery(id+"F1.wireOp",EDGE,"E19"),sQuery(id+"F1.wireOp",EDGE,"E20"),sQuery(id+"F1.wireOp",EDGE,"E23"),sQuery(id+"F1.wireOp",EDGE,"E24"),sQuery(id+"F1.wireOp",EDGE,"E25"),sQuery(id+"F1.wireOp",EDGE,"E26"),sQuery(id+"F1.wireOp",EDGE,"E27"),sQuery(id+"F1.wireOp",EDGE,"E28"),sQuery(id+"F1.wireOp",EDGE,"E29"),sQuery(id+"F1.wireOp",EDGE,"E30"),sQuery(id+"F1.wireOp",EDGE,"E31"),sQuery(id+"F1.wireOp",EDGE,"E32"),sQuery(id+"F1.wireOp",EDGE,"E33"),sQuery(id+"F1.wireOp",EDGE,"E34"),sQuery(id+"F1.wireOp",EDGE,"E35"),sQuery(id+"F1.wireOp",EDGE,"E36"),sQuery(id+"F1.wireOp",EDGE,"E37"),sQuery(id+"F1.wireOp",EDGE,"E38"),sQuery(id+"F1.wireOp",EDGE,"E39"),sQuery(id+"F1.wireOp",EDGE,"E40"),sQuery(id+"F1.wireOp",EDGE,"E41"),sQuery(id+"F1.wireOp",EDGE,"E42"),sQuery(id+"F1.wireOp",EDGE,"E46.rect.bottom"),sQuery(id+"F1.wireOp",EDGE,"E46.rect.top"),sQuery(id+"F1.wireOp",EDGE,"E46.rect.left"),sQuery(id+"F1.wireOp",EDGE,"E46.rect.right"),sQuery(id+"F1.wireOp",EDGE,"E47.top"),sQuery(id+"F1.wireOp",EDGE,"E48.bottom"),sQuery(id+"F1.wireOp",EDGE,"E49.bottom")])],"isStart":false}),makeQuery(id+"F5.opExtrude","SWEPT_FACE",FACE,{"disambiguationData":[OSD([sQuery(id+"F4.wireOp",EDGE,"E52.bottom")])]})]});
            var Q22;
            Q22=makeQuery(id+"F5.boolean.opBoolean","INTERSECT",EDGE,{"derivedFrom":[makeQuery(id+"F3.opExtrude","CAP_FACE",FACE,{"disambiguationData":[OSD([sQuery(id+"F1.wireOp",EDGE,"E13"),sQuery(id+"F1.wireOp",EDGE,"E15"),sQuery(id+"F1.wireOp",EDGE,"E16"),sQuery(id+"F1.wireOp",EDGE,"E18"),sQuery(id+"F1.wireOp",EDGE,"E19"),sQuery(id+"F1.wireOp",EDGE,"E20"),sQuery(id+"F1.wireOp",EDGE,"E23"),sQuery(id+"F1.wireOp",EDGE,"E24"),sQuery(id+"F1.wireOp",EDGE,"E25"),sQuery(id+"F1.wireOp",EDGE,"E26"),sQuery(id+"F1.wireOp",EDGE,"E27"),sQuery(id+"F1.wireOp",EDGE,"E28"),sQuery(id+"F1.wireOp",EDGE,"E29"),sQuery(id+"F1.wireOp",EDGE,"E30"),sQuery(id+"F1.wireOp",EDGE,"E31"),sQuery(id+"F1.wireOp",EDGE,"E32"),sQuery(id+"F1.wireOp",EDGE,"E33"),sQuery(id+"F1.wireOp",EDGE,"E34"),sQuery(id+"F1.wireOp",EDGE,"E35"),sQuery(id+"F1.wireOp",EDGE,"E36"),sQuery(id+"F1.wireOp",EDGE,"E37"),sQuery(id+"F1.wireOp",EDGE,"E38"),sQuery(id+"F1.wireOp",EDGE,"E39"),sQuery(id+"F1.wireOp",EDGE,"E40"),sQuery(id+"F1.wireOp",EDGE,"E41"),sQuery(id+"F1.wireOp",EDGE,"E42"),sQuery(id+"F1.wireOp",EDGE,"E46.rect.bottom"),sQuery(id+"F1.wireOp",EDGE,"E46.rect.top"),sQuery(id+"F1.wireOp",EDGE,"E46.rect.left"),sQuery(id+"F1.wireOp",EDGE,"E46.rect.right"),sQuery(id+"F1.wireOp",EDGE,"E47.top"),sQuery(id+"F1.wireOp",EDGE,"E48.bottom"),sQuery(id+"F1.wireOp",EDGE,"E49.bottom")])],"isStart":false}),makeQuery(id+"F5.opExtrude","SWEPT_FACE",FACE,{"disambiguationData":[OSD([sQuery(id+"F4.wireOp",EDGE,"E51.right")])]})]});
            var Q23;
            Q23=makeQuery(id+"F5.boolean.opBoolean","INTERSECT",EDGE,{"derivedFrom":[makeQuery(id+"F3.opExtrude","CAP_FACE",FACE,{"disambiguationData":[OSD([sQuery(id+"F1.wireOp",EDGE,"E13"),sQuery(id+"F1.wireOp",EDGE,"E15"),sQuery(id+"F1.wireOp",EDGE,"E16"),sQuery(id+"F1.wireOp",EDGE,"E18"),sQuery(id+"F1.wireOp",EDGE,"E19"),sQuery(id+"F1.wireOp",EDGE,"E20"),sQuery(id+"F1.wireOp",EDGE,"E23"),sQuery(id+"F1.wireOp",EDGE,"E24"),sQuery(id+"F1.wireOp",EDGE,"E25"),sQuery(id+"F1.wireOp",EDGE,"E26"),sQuery(id+"F1.wireOp",EDGE,"E27"),sQuery(id+"F1.wireOp",EDGE,"E28"),sQuery(id+"F1.wireOp",EDGE,"E29"),sQuery(id+"F1.wireOp",EDGE,"E30"),sQuery(id+"F1.wireOp",EDGE,"E31"),sQuery(id+"F1.wireOp",EDGE,"E32"),sQuery(id+"F1.wireOp",EDGE,"E33"),sQuery(id+"F1.wireOp",EDGE,"E34"),sQuery(id+"F1.wireOp",EDGE,"E35"),sQuery(id+"F1.wireOp",EDGE,"E36"),sQuery(id+"F1.wireOp",EDGE,"E37"),sQuery(id+"F1.wireOp",EDGE,"E38"),sQuery(id+"F1.wireOp",EDGE,"E39"),sQuery(id+"F1.wireOp",EDGE,"E40"),sQuery(id+"F1.wireOp",EDGE,"E41"),sQuery(id+"F1.wireOp",EDGE,"E42"),sQuery(id+"F1.wireOp",EDGE,"E46.rect.bottom"),sQuery(id+"F1.wireOp",EDGE,"E46.rect.top"),sQuery(id+"F1.wireOp",EDGE,"E46.rect.left"),sQuery(id+"F1.wireOp",EDGE,"E46.rect.right"),sQuery(id+"F1.wireOp",EDGE,"E47.top"),sQuery(id+"F1.wireOp",EDGE,"E48.bottom"),sQuery(id+"F1.wireOp",EDGE,"E49.bottom")])],"isStart":false}),makeQuery(id+"F5.opExtrude","SWEPT_FACE",FACE,{"disambiguationData":[OSD([sQuery(id+"F4.wireOp",EDGE,"E50.right")])]})]});
            var Q24;
            Q24=makeQuery(id+"F5.boolean.opBoolean","INTERSECT",EDGE,{"derivedFrom":[makeQuery(id+"F3.opExtrude","CAP_FACE",FACE,{"disambiguationData":[OSD([sQuery(id+"F1.wireOp",EDGE,"E13"),sQuery(id+"F1.wireOp",EDGE,"E15"),sQuery(id+"F1.wireOp",EDGE,"E16"),sQuery(id+"F1.wireOp",EDGE,"E18"),sQuery(id+"F1.wireOp",EDGE,"E19"),sQuery(id+"F1.wireOp",EDGE,"E20"),sQuery(id+"F1.wireOp",EDGE,"E23"),sQuery(id+"F1.wireOp",EDGE,"E24"),sQuery(id+"F1.wireOp",EDGE,"E25"),sQuery(id+"F1.wireOp",EDGE,"E26"),sQuery(id+"F1.wireOp",EDGE,"E27"),sQuery(id+"F1.wireOp",EDGE,"E28"),sQuery(id+"F1.wireOp",EDGE,"E29"),sQuery(id+"F1.wireOp",EDGE,"E30"),sQuery(id+"F1.wireOp",EDGE,"E31"),sQuery(id+"F1.wireOp",EDGE,"E32"),sQuery(id+"F1.wireOp",EDGE,"E33"),sQuery(id+"F1.wireOp",EDGE,"E34"),sQuery(id+"F1.wireOp",EDGE,"E35"),sQuery(id+"F1.wireOp",EDGE,"E36"),sQuery(id+"F1.wireOp",EDGE,"E37"),sQuery(id+"F1.wireOp",EDGE,"E38"),sQuery(id+"F1.wireOp",EDGE,"E39"),sQuery(id+"F1.wireOp",EDGE,"E40"),sQuery(id+"F1.wireOp",EDGE,"E41"),sQuery(id+"F1.wireOp",EDGE,"E42"),sQuery(id+"F1.wireOp",EDGE,"E46.rect.bottom"),sQuery(id+"F1.wireOp",EDGE,"E46.rect.top"),sQuery(id+"F1.wireOp",EDGE,"E46.rect.left"),sQuery(id+"F1.wireOp",EDGE,"E46.rect.right"),sQuery(id+"F1.wireOp",EDGE,"E47.top"),sQuery(id+"F1.wireOp",EDGE,"E48.bottom"),sQuery(id+"F1.wireOp",EDGE,"E49.bottom")])],"isStart":false}),makeQuery(id+"F5.opExtrude","SWEPT_FACE",FACE,{"disambiguationData":[OSD([sQuery(id+"F4.wireOp",EDGE,"E55.top")])]})]});
            var Q25;
            {var subQ0=sQuery(id+"F4.wireOp",EDGE,"E56.left");Q25=makeQuery(id+"F6.boolean.opBoolean","MERGE",EDGE,{"derivedFrom":[makeQuery(id+"F5.boolean.opBoolean","INTERSECT",EDGE,{"derivedFrom":[makeQuery(id+"F3.opExtrude","CAP_FACE",FACE,{"disambiguationData":[OSD([sQuery(id+"F1.wireOp",EDGE,"E13"),sQuery(id+"F1.wireOp",EDGE,"E15"),sQuery(id+"F1.wireOp",EDGE,"E16"),sQuery(id+"F1.wireOp",EDGE,"E18"),sQuery(id+"F1.wireOp",EDGE,"E19"),sQuery(id+"F1.wireOp",EDGE,"E20"),sQuery(id+"F1.wireOp",EDGE,"E23"),sQuery(id+"F1.wireOp",EDGE,"E24"),sQuery(id+"F1.wireOp",EDGE,"E25"),sQuery(id+"F1.wireOp",EDGE,"E26"),sQuery(id+"F1.wireOp",EDGE,"E27"),sQuery(id+"F1.wireOp",EDGE,"E28"),sQuery(id+"F1.wireOp",EDGE,"E29"),sQuery(id+"F1.wireOp",EDGE,"E30"),sQuery(id+"F1.wireOp",EDGE,"E31"),sQuery(id+"F1.wireOp",EDGE,"E32"),sQuery(id+"F1.wireOp",EDGE,"E33"),sQuery(id+"F1.wireOp",EDGE,"E34"),sQuery(id+"F1.wireOp",EDGE,"E35"),sQuery(id+"F1.wireOp",EDGE,"E36"),sQuery(id+"F1.wireOp",EDGE,"E37"),sQuery(id+"F1.wireOp",EDGE,"E38"),sQuery(id+"F1.wireOp",EDGE,"E39"),sQuery(id+"F1.wireOp",EDGE,"E40"),sQuery(id+"F1.wireOp",EDGE,"E41"),sQuery(id+"F1.wireOp",EDGE,"E42"),sQuery(id+"F1.wireOp",EDGE,"E46.rect.bottom"),sQuery(id+"F1.wireOp",EDGE,"E46.rect.top"),sQuery(id+"F1.wireOp",EDGE,"E46.rect.left"),sQuery(id+"F1.wireOp",EDGE,"E46.rect.right"),sQuery(id+"F1.wireOp",EDGE,"E47.top"),sQuery(id+"F1.wireOp",EDGE,"E48.bottom"),sQuery(id+"F1.wireOp",EDGE,"E49.bottom")])],"isStart":false}),makeQuery(id+"F5.opExtrude","SWEPT_FACE",FACE,{"disambiguationData":[OSD([sQuery(id+"F4.wireOp",EDGE,"E55.right"),subQ0])]})]}),makeQuery(id+"F6.opExtrude","CAP_EDGE",EDGE,{"disambiguationData":[OSD([subQ0])],"isStart":false})]});}
            var Q26;
            {var subQ0=sQuery(id+"F4.wireOp",EDGE,"E54.left");Q26=makeQuery(id+"F6.boolean.opBoolean","MERGE",EDGE,{"derivedFrom":[makeQuery(id+"F5.boolean.opBoolean","INTERSECT",EDGE,{"derivedFrom":[makeQuery(id+"F3.opExtrude","CAP_FACE",FACE,{"disambiguationData":[OSD([sQuery(id+"F1.wireOp",EDGE,"E13"),sQuery(id+"F1.wireOp",EDGE,"E15"),sQuery(id+"F1.wireOp",EDGE,"E16"),sQuery(id+"F1.wireOp",EDGE,"E18"),sQuery(id+"F1.wireOp",EDGE,"E19"),sQuery(id+"F1.wireOp",EDGE,"E20"),sQuery(id+"F1.wireOp",EDGE,"E23"),sQuery(id+"F1.wireOp",EDGE,"E24"),sQuery(id+"F1.wireOp",EDGE,"E25"),sQuery(id+"F1.wireOp",EDGE,"E26"),sQuery(id+"F1.wireOp",EDGE,"E27"),sQuery(id+"F1.wireOp",EDGE,"E28"),sQuery(id+"F1.wireOp",EDGE,"E29"),sQuery(id+"F1.wireOp",EDGE,"E30"),sQuery(id+"F1.wireOp",EDGE,"E31"),sQuery(id+"F1.wireOp",EDGE,"E32"),sQuery(id+"F1.wireOp",EDGE,"E33"),sQuery(id+"F1.wireOp",EDGE,"E34"),sQuery(id+"F1.wireOp",EDGE,"E35"),sQuery(id+"F1.wireOp",EDGE,"E36"),sQuery(id+"F1.wireOp",EDGE,"E37"),sQuery(id+"F1.wireOp",EDGE,"E38"),sQuery(id+"F1.wireOp",EDGE,"E39"),sQuery(id+"F1.wireOp",EDGE,"E40"),sQuery(id+"F1.wireOp",EDGE,"E41"),sQuery(id+"F1.wireOp",EDGE,"E42"),sQuery(id+"F1.wireOp",EDGE,"E46.rect.bottom"),sQuery(id+"F1.wireOp",EDGE,"E46.rect.top"),sQuery(id+"F1.wireOp",EDGE,"E46.rect.left"),sQuery(id+"F1.wireOp",EDGE,"E46.rect.right"),sQuery(id+"F1.wireOp",EDGE,"E47.top"),sQuery(id+"F1.wireOp",EDGE,"E48.bottom"),sQuery(id+"F1.wireOp",EDGE,"E49.bottom")])],"isStart":false}),makeQuery(id+"F5.opExtrude","SWEPT_FACE",FACE,{"disambiguationData":[OSD([sQuery(id+"F4.wireOp",EDGE,"E53.right"),subQ0])]})]}),makeQuery(id+"F6.opExtrude","CAP_EDGE",EDGE,{"disambiguationData":[OSD([subQ0])],"isStart":false})]});}
            var Q27;
            Q27=makeQuery(id+"F5.boolean.opBoolean","INTERSECT",EDGE,{"derivedFrom":[makeQuery(id+"F3.opExtrude","CAP_FACE",FACE,{"disambiguationData":[OSD([sQuery(id+"F1.wireOp",EDGE,"E13"),sQuery(id+"F1.wireOp",EDGE,"E15"),sQuery(id+"F1.wireOp",EDGE,"E16"),sQuery(id+"F1.wireOp",EDGE,"E18"),sQuery(id+"F1.wireOp",EDGE,"E19"),sQuery(id+"F1.wireOp",EDGE,"E20"),sQuery(id+"F1.wireOp",EDGE,"E23"),sQuery(id+"F1.wireOp",EDGE,"E24"),sQuery(id+"F1.wireOp",EDGE,"E25"),sQuery(id+"F1.wireOp",EDGE,"E26"),sQuery(id+"F1.wireOp",EDGE,"E27"),sQuery(id+"F1.wireOp",EDGE,"E28"),sQuery(id+"F1.wireOp",EDGE,"E29"),sQuery(id+"F1.wireOp",EDGE,"E30"),sQuery(id+"F1.wireOp",EDGE,"E31"),sQuery(id+"F1.wireOp",EDGE,"E32"),sQuery(id+"F1.wireOp",EDGE,"E33"),sQuery(id+"F1.wireOp",EDGE,"E34"),sQuery(id+"F1.wireOp",EDGE,"E35"),sQuery(id+"F1.wireOp",EDGE,"E36"),sQuery(id+"F1.wireOp",EDGE,"E37"),sQuery(id+"F1.wireOp",EDGE,"E38"),sQuery(id+"F1.wireOp",EDGE,"E39"),sQuery(id+"F1.wireOp",EDGE,"E40"),sQuery(id+"F1.wireOp",EDGE,"E41"),sQuery(id+"F1.wireOp",EDGE,"E42"),sQuery(id+"F1.wireOp",EDGE,"E46.rect.bottom"),sQuery(id+"F1.wireOp",EDGE,"E46.rect.top"),sQuery(id+"F1.wireOp",EDGE,"E46.rect.left"),sQuery(id+"F1.wireOp",EDGE,"E46.rect.right"),sQuery(id+"F1.wireOp",EDGE,"E47.top"),sQuery(id+"F1.wireOp",EDGE,"E48.bottom"),sQuery(id+"F1.wireOp",EDGE,"E49.bottom")])],"isStart":false}),makeQuery(id+"F5.opExtrude","SWEPT_FACE",FACE,{"disambiguationData":[OSD([sQuery(id+"F4.wireOp",EDGE,"E53.top")])]})]});
            var Q28;
            Q28=makeQuery(id+"F5.opExtrude","SWEPT_EDGE",EDGE,{"disambiguationData":[OSD([sQuery(id+"F4.wireOp",EDGE,"E55.top"),sQuery(id+"F4.wireOp",EDGE,"E55.right")])]});
            var Q29;
            Q29=makeQuery(id+"F5.opExtrude","SWEPT_EDGE",EDGE,{"disambiguationData":[OSD([sQuery(id+"F4.wireOp",EDGE,"E53.top"),sQuery(id+"F4.wireOp",EDGE,"E53.right")])]});
            var Q30;
            Q30=makeQuery(id+"F3BZSZNoRLu20LP_1.1.F14.opExtrude","CAP_EDGE",EDGE,{"disambiguationData":[OSD([sQuery(id+"F13.wireOp",EDGE,"E65")])],"isStart":true});
            var Q31;
            Q31=makeQuery(id+"F5.opExtrude","SWEPT_EDGE",EDGE,{"disambiguationData":[OSD([sQuery(id+"F4.wireOp",EDGE,"E50.top"),sQuery(id+"F4.wireOp",EDGE,"E50.right"),sQuery(id+"F4.wireOp",EDGE,"E52.bottom")])]});
            var Q32;
            Q32=makeQuery(id+"F5.opExtrude","CAP_EDGE",EDGE,{"disambiguationData":[OSD([sQuery(id+"F4.wireOp",EDGE,"E53.right"),sQuery(id+"F4.wireOp",EDGE,"E54.left")])],"isStart":false});
            var Q33;
            Q33=makeQuery(id+"F5.opExtrude","CAP_EDGE",EDGE,{"disambiguationData":[OSD([sQuery(id+"F4.wireOp",EDGE,"E55.right"),sQuery(id+"F4.wireOp",EDGE,"E56.left")])],"isStart":false});
            var Q34;
            Q34=makeQuery(id+"F3BZSZNoRLu20LP_1.1.F14.opExtrude","CAP_FACE",FACE,{"disambiguationData":[OSD([sQuery(id+"F13.wireOp",EDGE,"E68"),sQuery(id+"F13.wireOp",EDGE,"E69"),sQuery(id+"F13.wireOp",EDGE,"E70")])],"isStart":false});
            fillet(context, id + "F16", {"entities" : qUnion([Q0, Q1, Q2, Q3, Q4, Q5, Q6, Q7, Q8, Q9, Q10, Q11, Q12, Q13, Q14, Q15, Q16, Q17, Q18, Q19, Q20, Q21, Q22, Q23, Q24, Q25, Q26, Q27, Q28, Q29, Q30, Q31, Q32, Q33, Q34]), "radius" : 2 * mm, "tangentPropagation" : true, "allowEdgeOverflow" : false});
        }
    });
